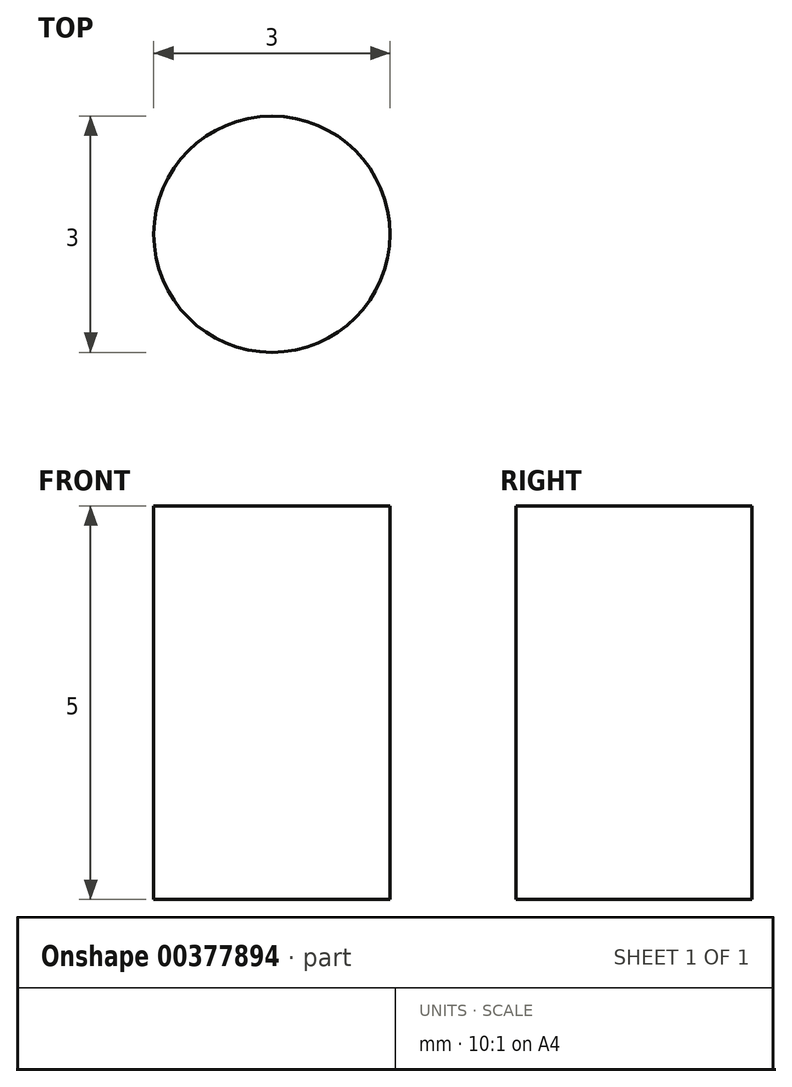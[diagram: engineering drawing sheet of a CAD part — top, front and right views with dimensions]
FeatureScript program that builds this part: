
annotation { "Feature Type Name" : "Feature", "Feature Type Description" : "" }
export const myFeature = defineFeature(function(context is Context, id is Id, definition is map)
    precondition{}
    {
        {
            var Q0;
            Q0=qCreatedBy(makeId("Top.planeOp"),FACE);
            var sketch = newSketch(context, id + "F0", { "sketchPlane" : qUnion([Q0])});
            skCircle(sketch, "E0", {"center": v(0, 0) * mm, "radius": 1.5 * mm});
            skSolve(sketch);
        }
        {
            var Q0;
            Q0 = qSketchRegion(id + "F0", true);
            extrude(context, id + "F1", {"entities" : qUnion([Q0]), "depth" : 5 * mm});
        }
    });
